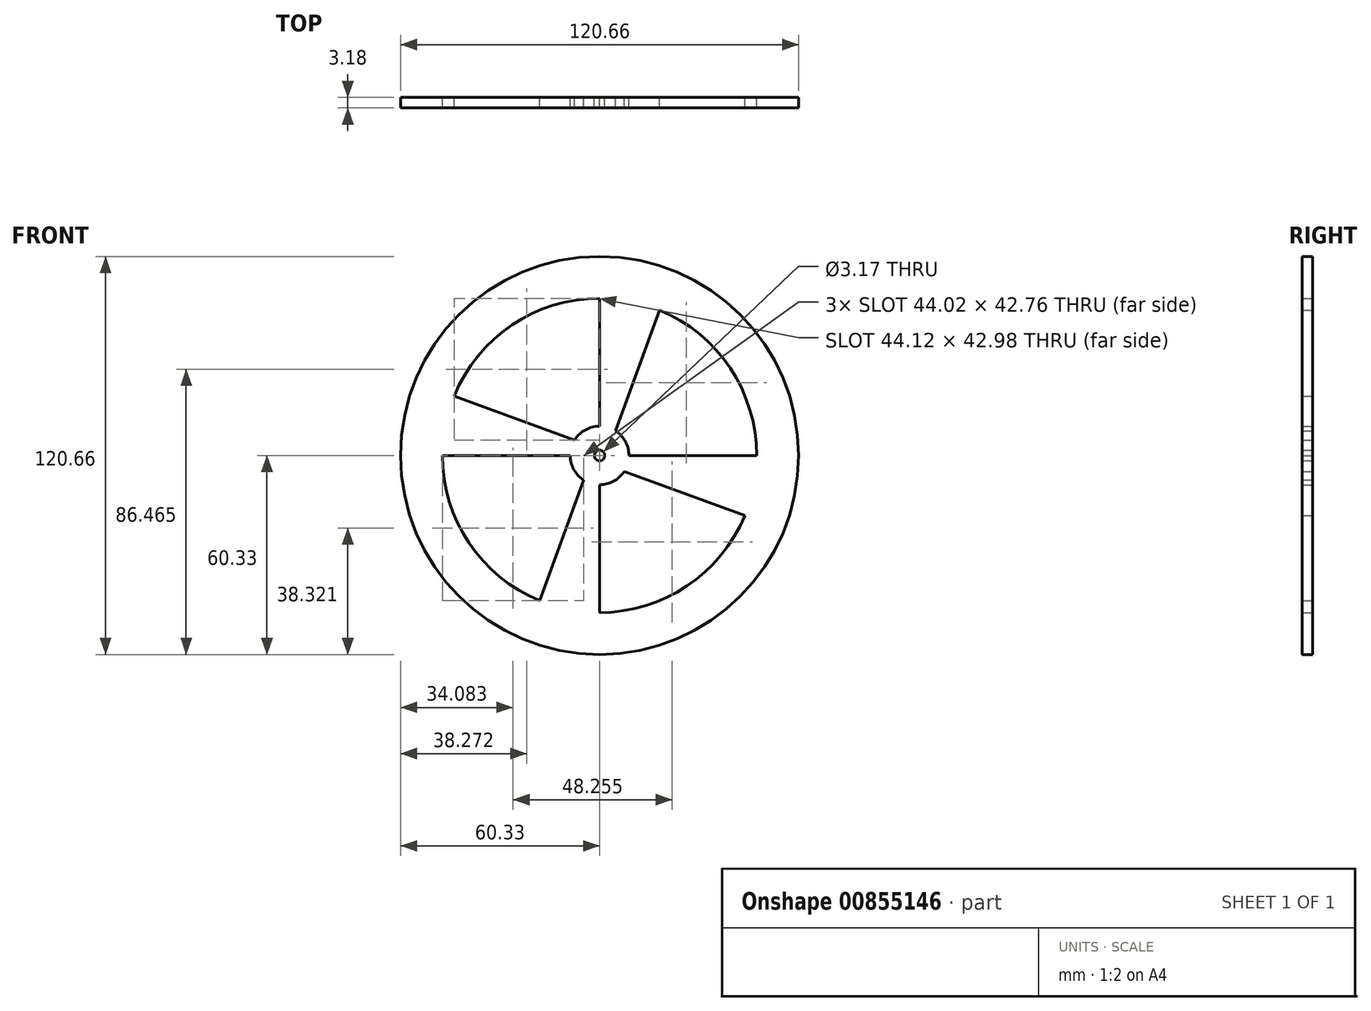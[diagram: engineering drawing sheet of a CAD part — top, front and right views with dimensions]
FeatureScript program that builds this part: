
annotation { "Feature Type Name" : "Feature", "Feature Type Description" : "" }
export const myFeature = defineFeature(function(context is Context, id is Id, definition is map)
    precondition{}
    {
        {
            var Q0;
            Q0=qCreatedBy(makeId("Front.planeOp"),FACE);
            var sketch = newSketch(context, id + "F0", { "sketchPlane" : qUnion([Q0])});
            skCircle(sketch, "E0", {"center": v(0, 0) * mm, "radius": 60.33 * mm});
            skArc(sketch, "E1", {"start": v(-47.62, 0) * mm, "mid": v(-39.59, -26.48) * mm, "end": v(-18.18, -44.02) * mm});
            skArc(sketch, "E2", {"start": v(0, 8.9) * mm, "mid": v(-4.34, 7.76) * mm, "end": v(-7.58, 4.64) * mm});
            skCircle(sketch, "E3", {"center": v(0, 0) * mm, "radius": 1.59 * mm});
            skLineSegment(sketch, "E4", {"start": v(0, 47.62) * mm, "end": v(0, 8.89) * mm});
            skLineSegment(sketch, "E5", {"start": v(4.87, 7.44) * mm, "end": v(18.18, 44.02) * mm});
            skLineSegment(sketch, "E6", {"start": v(8.89, 0) * mm, "end": v(47.62, 0) * mm});
            skLineSegment(sketch, "E7", {"start": v(7.44, -4.87) * mm, "end": v(44.02, -18.18) * mm});
            skLineSegment(sketch, "E8", {"start": v(0, -8.89) * mm, "end": v(0, -47.62) * mm});
            skLineSegment(sketch, "E9", {"start": v(-4.87, -7.44) * mm, "end": v(-18.18, -44.02) * mm});
            skLineSegment(sketch, "E10", {"start": v(-8.89, 0) * mm, "end": v(-47.62, 0) * mm});
            skArc(sketch, "E11.trimOffspring", {"start": v(0, 47.62) * mm, "mid": v(-26.59, 39.51) * mm, "end": v(-44.12, 17.94) * mm});
            skArc(sketch, "E12.trimOffspring", {"start": v(47.62, 0) * mm, "mid": v(39.59, 26.48) * mm, "end": v(18.18, 44.02) * mm});
            skArc(sketch, "E13.trimOffspring", {"start": v(0, -47.62) * mm, "mid": v(26.48, -39.59) * mm, "end": v(44.02, -18.18) * mm});
            skLineSegment(sketch, "E14", {"start": v(-44.12, 17.94) * mm, "end": v(-7.58, 4.64) * mm});
            skArc(sketch, "E15.trimOffspring", {"start": v(-8.9, 0) * mm, "mid": v(-7.82, -4.23) * mm, "end": v(-4.87, -7.44) * mm});
            skArc(sketch, "E16.trimOffspring", {"start": v(0, -8.9) * mm, "mid": v(4.23, -7.82) * mm, "end": v(7.44, -4.87) * mm});
            skArc(sketch, "E17.trimOffspring", {"start": v(8.9, 0) * mm, "mid": v(7.82, 4.23) * mm, "end": v(4.87, 7.44) * mm});
            skSolve(sketch);
        }
        {
            var Q0;
            Q0=makeQuery(id+"F0.imprint","IMPRINT",FACE,{"disambiguationData":[TD([[makeQuery(id+"F0.imprint","IMPRINT",EDGE,{"derivedFrom":sQuery(id+"F0.wireOp",EDGE,"E0")}),1.0]])]});
            extrude(context, id + "F1", {"entities" : qUnion([Q0]), "depth" : 3.17 * mm, "offsetDistance" : 25.4 * mm});
        }
    });
